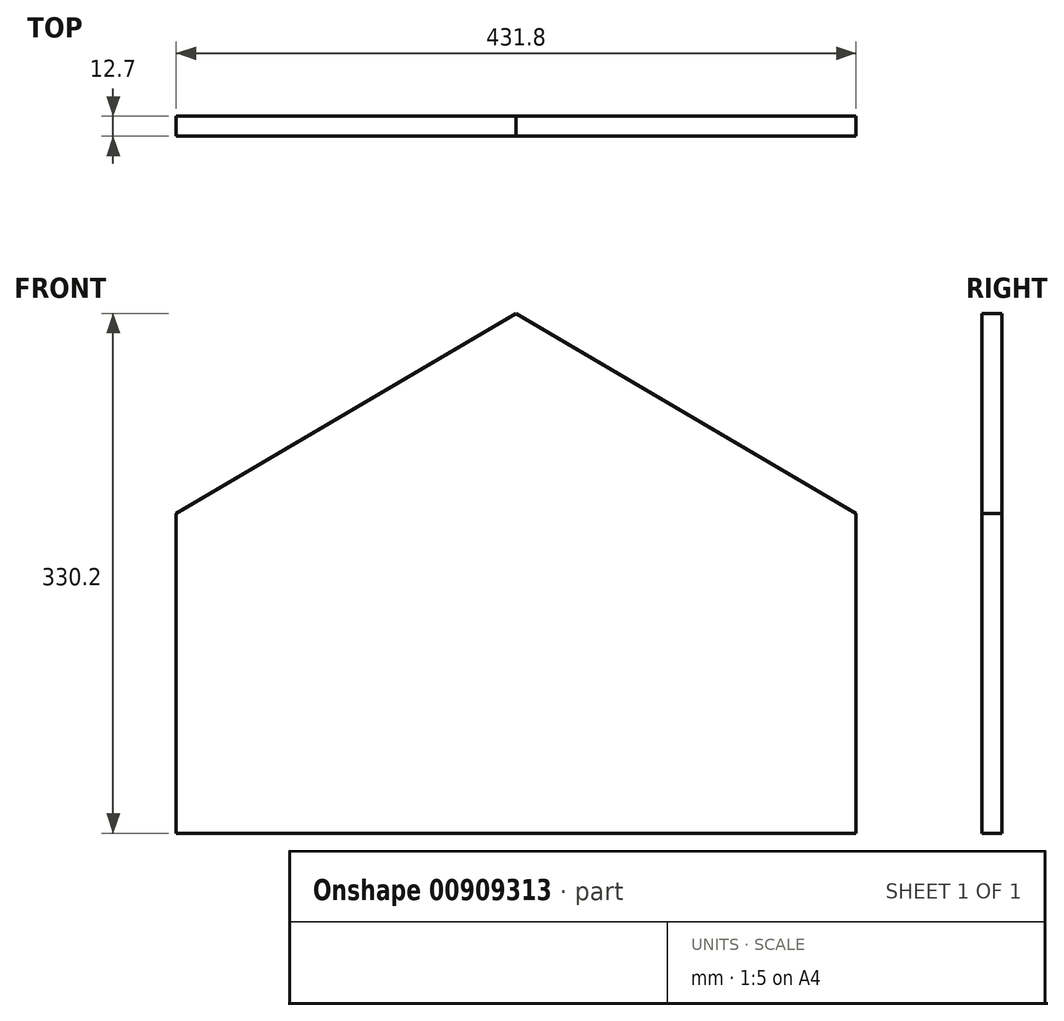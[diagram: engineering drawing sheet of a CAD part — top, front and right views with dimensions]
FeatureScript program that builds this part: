
annotation { "Feature Type Name" : "Feature", "Feature Type Description" : "" }
export const myFeature = defineFeature(function(context is Context, id is Id, definition is map)
    precondition{}
    {
        {
            var Q0;
            Q0=qCreatedBy(makeId("Front.planeOp"),FACE);
            var sketch = newSketch(context, id + "F0", { "sketchPlane" : qUnion([Q0])});
            skLineSegment(sketch, "E0.bottom", {"start": v(-215.9, -101.6) * mm, "end": v(215.9, -101.6) * mm});
            skLineSegment(sketch, "E0.left", {"start": v(-215.9, -101.6) * mm, "end": v(-215.9, 101.6) * mm});
            skLineSegment(sketch, "E0.right", {"start": v(215.9, -101.6) * mm, "end": v(215.9, 101.6) * mm});
            skPoint(sketch, "E0.middle", {"position": v(0, 0) * mm});
            skLineSegment(sketch, "E1", {"start": v(0, 228.6) * mm, "end": v(-215.9, 101.6) * mm});
            skLineSegment(sketch, "E2", {"start": v(0, 228.6) * mm, "end": v(215.9, 101.6) * mm});
            skPoint(sketch, "E3.end.orphan", {"position": v(0, 101.6) * mm});
            skSolve(sketch);
        }
        {
            var Q0;
            Q0=makeQuery(id+"F0.imprint","IMPRINT",FACE,{"disambiguationData":[TD([[makeQuery(id+"F0.imprint","IMPRINT",EDGE,{"derivedFrom":sQuery(id+"F0.wireOp",EDGE,"E0.bottom")}),1.0]])]});
            extrude(context, id + "F1", {"entities" : qUnion([Q0]), "depth" : 12.7 * mm, "offsetDistance" : 25.4 * mm});
        }
    });
